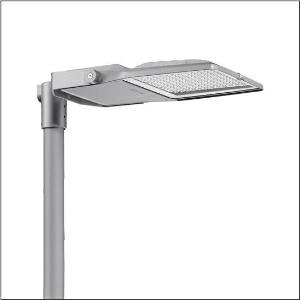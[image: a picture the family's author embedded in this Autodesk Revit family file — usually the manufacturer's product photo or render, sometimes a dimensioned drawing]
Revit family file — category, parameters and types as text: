
# Revit family: floodlight_fl_21_iq_midi___pl43_5xa7781e4a3a_24f4
name_source: partatom
category: Lighting Fixtures
units: mm (PartAtom-declared; Revit-internal decimal feet)

## family parameters
Cut with Voids When Loaded = No
Host = Face
Light Source = No
Part Type = Normal
Room Calculation Point = No
Round Connector Dimension = Use Diameter
Shared = No

## types (1)
- --- (1 x LED, 28730 lm, 208.1 W, 4000K)
    Apparent Load = 208 VA
    CIE Flux Codes = 27 78 99 100 100
    Color Rendering = 70
    Color Temperature = 4000K
    Default Elevation = 1800 mm
    Description = Floodlight FL 21 iQ midi, floodlight, primary light control with lens, of PMMA, primary optical cover: protective disc, of toughened safety glass, transparent, light distribution: PL43, light emission: direct distribution, installation type: surface-mounted, LED, High Power LED, rated luminous flux: 28.730lm, luminous efficacy: 138lm/W, light colour: 740, colour temperature: 4000K, control gear: ECG iQ, control: optimised constant luminous flux control (CLO 2.0), Desk-Remote (wireless, voltage-free reading and setting of iQ features in the workshop via application-optimized NFC function/RFID function), Light-Fading, Smart-Wire, Night-Set, Lumen-Switch, Temp-Guard, Auto-Match, with terminal, 6-pole, mains connection: 220..240V, AC, 50/60Hz, start of lifetime: 208W, end of service life: 227W, reduction: 90W, luminaire housing, of diecast aluminium, powder-coated, Siteco® metallic grey (DB 702S), corrosivity category C5 mid according to DIN EN ISO 12944, sealing non-destructively replaceable, please order mast flange separately, mast bracket, of steel, galvanised, powder-coated, Siteco® metallic grey (DB 702S), protection rating (complete): IP66, insulation class (complete): insulation class II (safety insulation), certification: CE, protection symbol: D, impact resistance: IK08, permissible operating ambient temperature: -40..+40°C, permissible operating ambient temperature for outdoor applications: -40..+50°C, standard: DIN EN 12944, LABS conformity tested according to VDMA 24364:2018-05, packaging unit: 1 piece

Light Distribution: PL43
    Height = 76 mm
    Lamp = 1 x LED
    Lamp Light Flux = 28730 lm
    Lamp Power = 208.1 W
    Lamp count = 1
    Length = 657 mm
    Luminous efficacy = 138 lm/W
    Manufacturer = Siteco
    ModVariant = No
    Model = 5XA7781E4A3A
    Number of Poles = 1
    OnlyDefault = Yes
    Power Factor = 1
    Product Name = Floodlight FL 21 iQ midi | PL43
    Product group = floodlight | pylon annexe
    ProductGroupID = 6200
    Protection Class = Protection class II
    Protection Degree = IP 66
    RLX_Detail_Level = 1
    RLX_Emergency_Light_Flux = 0 lm
    RLX_Emergency_Type = 0
    RLX_Emergency_Type_DB = No
    RlxData = <blob elided: 153641 chars, md5=f3adb878>
    Socket = socket
    Standby Power = 0 W
    System Light Flux = 28730 lm
    System Power = 208 W
    Type Comments = factory setting: luminous flux: 100 % | dim-lin: 254 | 710 mA
    Type Image = l_1007123.jpg
    URL = http://relux.com
    VarID = @adj_035427
    Voltage = 0 V
    Weight = 0.00 kg
    Width = 442 mm

## geometry (parser evidence)
native form markers: Blend x4, Sweep x17
no freeform markers — native parametric forms only
